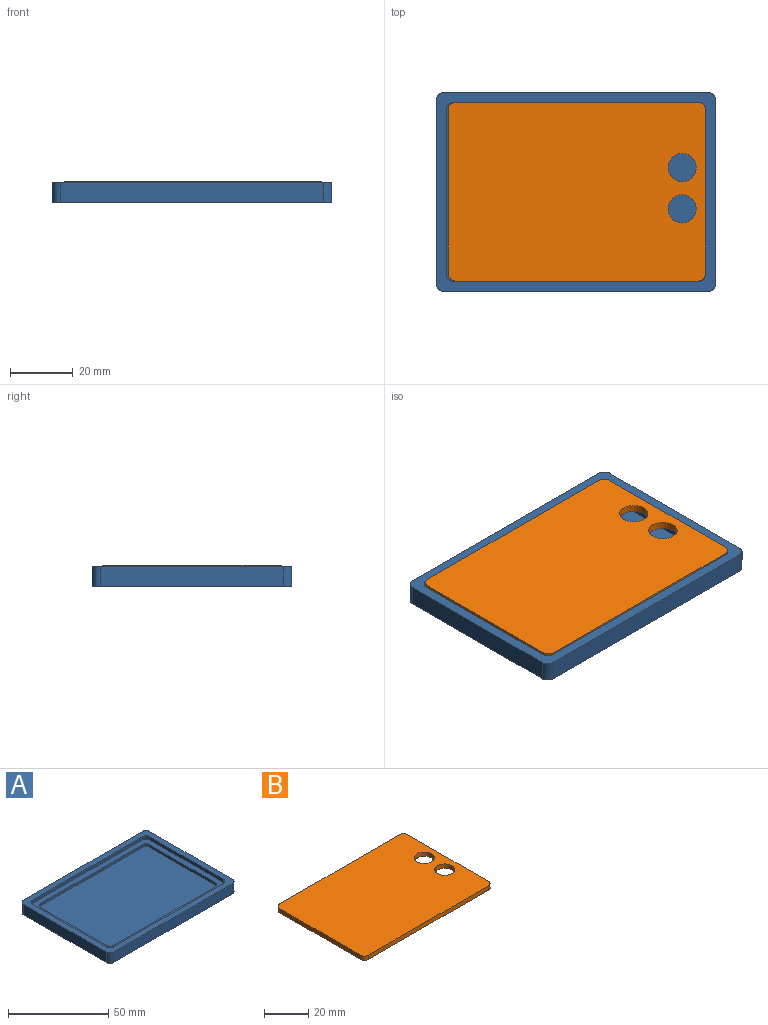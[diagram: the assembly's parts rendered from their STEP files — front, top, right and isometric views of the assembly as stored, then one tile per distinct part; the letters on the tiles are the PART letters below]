
ASSEMBLY  parts=2 mates=1
PART A: 28 faces, bbox 88.9x63.5x6.4 mm
  f0: plane 82.55x57.15mm, normal (0,0,1), area 782mm2, adj f11,f12,f13,f14,f15,f16,f17,f18
  f1: plane 88.9x63.5mm, normal (0,0,1), area 927.4mm2, adj f2,f3,f4,f5,f7,f8,f9,f10
  f2: plane 83.82x6.35mm, normal (0,1,0), area 532.3mm2, adj f1,f6,f7,f10
  f3: plane 58.42x6.35mm, normal (-1,0,0), area 371mm2, adj f1,f6,f7,f8
  f4: plane 83.82x6.35mm, normal (0,-1,0), area 532.3mm2, adj f1,f6,f8,f9
  f5: plane 58.42x6.35mm, normal (1,0,0), area 371mm2, adj f1,f6,f9,f10
  f6: plane 88.9x63.5mm, normal (0,0,-1), area 5639.6mm2, adj f2,f3,f4,f5,f7,f8,f9,f10
  f7: cylinder r=2.54mm len=6.35mm, axis (0,0,1), area 25.3mm2, adj f1,f2,f3,f6
  f8: cylinder r=2.54mm len=6.35mm, axis (0,0,-1), area 25.3mm2, adj f1,f3,f4,f6
  f9: cylinder r=2.54mm len=6.35mm, axis (0,0,1), area 25.3mm2, adj f1,f4,f5,f6
  f10: cylinder r=2.54mm len=6.35mm, axis (0,0,-1), area 25.3mm2, adj f1,f2,f5,f6
  f11: plane 52.07x2mm, normal (-1,0,0), area 104.1mm2, adj f0,f1,f12,f18
  f12: cylinder r=2.54mm len=2.54mm, axis (0,0,1), area 8mm2, adj f0,f1,f11,f13
  f13: plane 77.47x2mm, normal (0,-1,0), area 154.9mm2, adj f0,f1,f12,f14
  f14: cylinder r=2.54mm len=2.54mm, axis (0,0,1), area 8mm2, adj f0,f1,f13,f15
  f15: plane 52.07x2mm, normal (1,0,0), area 104.1mm2, adj f0,f1,f14,f16
  f16: cylinder r=2.54mm len=2.54mm, axis (0,0,1), area 8mm2, adj f0,f1,f15,f17
  f17: plane 77.47x2mm, normal (0,1,0), area 154.9mm2, adj f0,f1,f16,f18
  f18: cylinder r=2.54mm len=2.54mm, axis (0,0,1), area 8mm2, adj f0,f1,f11,f17
  f19: plane 46.23x1.63mm, normal (-1,0,0), area 75.1mm2, adj f0,f20,f26,f27
  f20: cylinder r=2.54mm len=2.54mm, axis (0,0,1), area 6.5mm2, adj f0,f19,f21,f27
  f21: plane 71.63x1.63mm, normal (0,-1,0), area 116.4mm2, adj f0,f20,f22,f27
  f22: cylinder r=2.54mm len=2.54mm, axis (0,0,1), area 6.5mm2, adj f0,f21,f23,f27
  f23: plane 46.23x1.63mm, normal (1,0,0), area 75.1mm2, adj f0,f22,f24,f27
  f24: cylinder r=2.54mm len=2.54mm, axis (0,0,1), area 6.5mm2, adj f0,f23,f25,f27
  f25: plane 71.63x1.63mm, normal (0,1,0), area 116.4mm2, adj f0,f24,f26,f27
  f26: cylinder r=2.54mm len=2.54mm, axis (0,0,1), area 6.5mm2, adj f0,f19,f25,f27
  f27: plane 76.71x51.31mm, normal (0,0,1), area 3930.2mm2, adj f19,f20,f21,f22,f23,f24,f25,f26
PART B: 12 faces, bbox 82x57x2.4 mm
  f0: plane 76.92x2.35mm, normal (0,1,0), area 180.8mm2, adj f4,f5,f6,f9
  f1: plane 51.87x2.35mm, normal (-1,0,0), area 121.9mm2, adj f4,f5,f6,f7
  f2: plane 76.92x2.35mm, normal (0,-1,0), area 180.8mm2, adj f4,f5,f7,f8
  f3: plane 51.87x2.35mm, normal (1,0,0), area 121.9mm2, adj f4,f5,f8,f9
  f4: plane 82x56.95mm, normal (0,0,1), area 4537.1mm2, adj f0,f1,f2,f3,f6,f7,f8,f9
  f5: plane 82x56.95mm, normal (0,0,-1), area 4537.1mm2, adj f0,f1,f2,f3,f6,f7,f8,f9
  f6: cylinder r=2.54mm len=2.54mm, axis (0,0,1), area 9.4mm2, adj f0,f1,f4,f5
  f7: cylinder r=2.54mm len=2.54mm, axis (0,0,-1), area 9.4mm2, adj f1,f2,f4,f5
  f8: cylinder r=2.54mm len=2.54mm, axis (0,0,1), area 9.4mm2, adj f2,f3,f4,f5
  f9: cylinder r=2.54mm len=2.54mm, axis (0,0,-1), area 9.4mm2, adj f0,f3,f4,f5
  f10: cylinder r=4.5mm len=9mm, axis (0,0,1), area 66.4mm2, adj f4,f5
  f11: cylinder r=4.5mm len=9mm, axis (0,0,1), area 66.4mm2, adj f4,f5
PLACE A t=(-94.64,7.03,-28.7)mm
PLACE B t=(-94.36,7.13,-24.35)mm
MATE revolute A.f12 <-> B.f9  axis (0,0,1) through (-55.9,33.07,-24.35)mm
